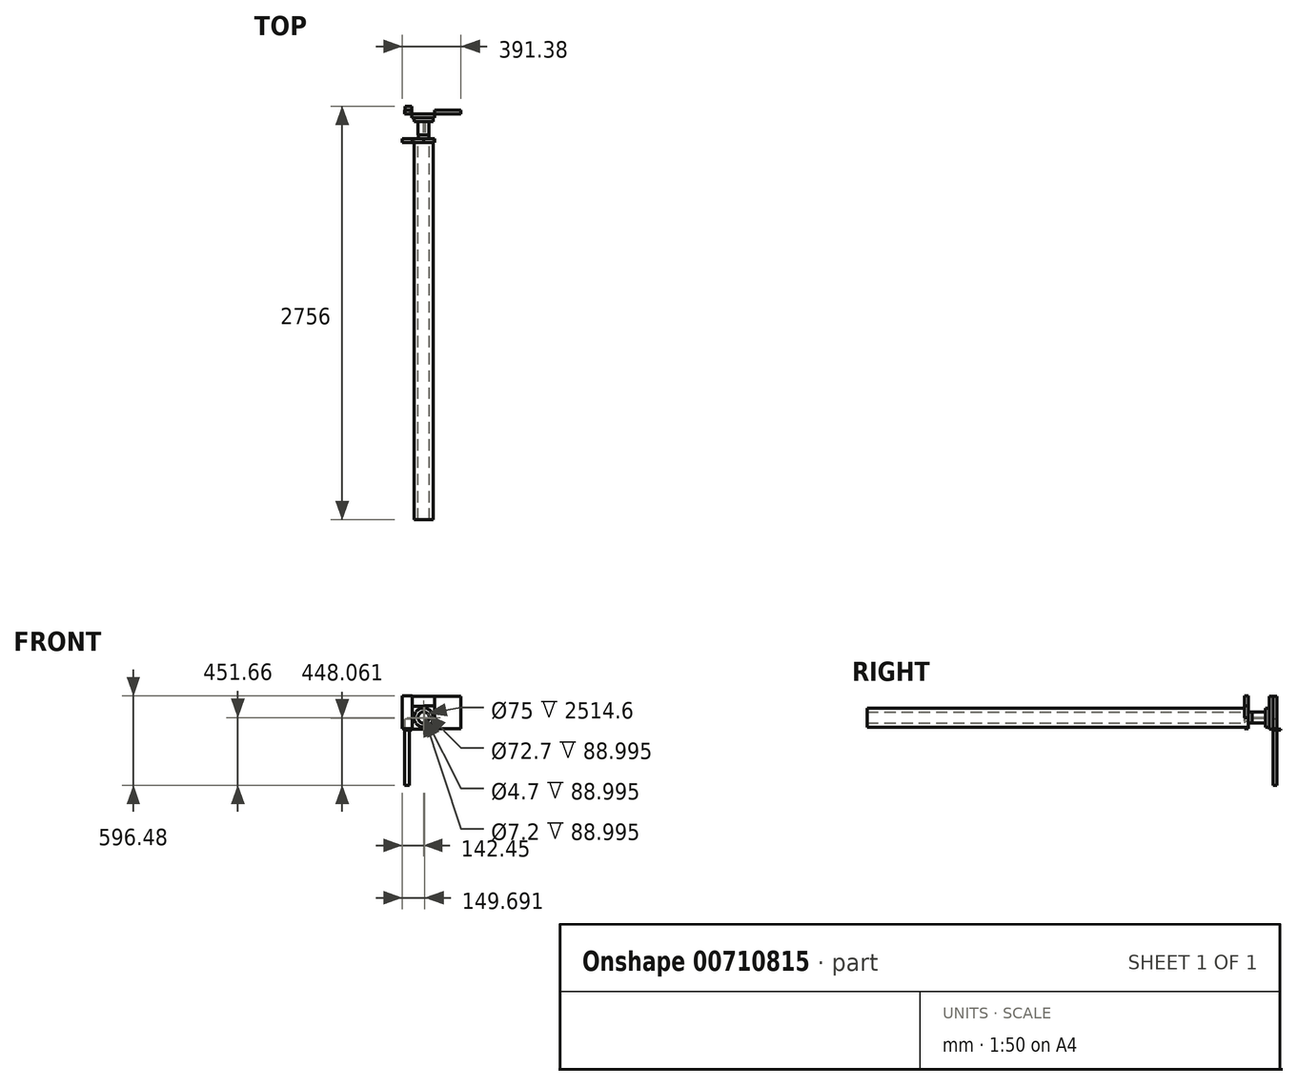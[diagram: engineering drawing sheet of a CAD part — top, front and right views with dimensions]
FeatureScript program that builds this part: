
annotation { "Feature Type Name" : "Feature", "Feature Type Description" : "" }
export const myFeature = defineFeature(function(context is Context, id is Id, definition is map)
    precondition{}
    {
        {
            var Q0;
            Q0=qCreatedBy(makeId("Front.planeOp"),FACE);
            var sketch = newSketch(context, id + "F0", { "sketchPlane" : qUnion([Q0])});
            skCircle(sketch, "E0", {"center": v(0, 0) * mm, "radius": 63.5 * mm});
            skSolve(sketch);
        }
        {
            var Q0;
            Q0 = qSketchRegion(id + "F0", true);
            extrude(context, id + "F1", {"entities" : qUnion([Q0]), "depth" : 2540 * mm, "offsetDistance" : 25.4 * mm});
        }
        {
            var Q0;
            Q0=makeQuery(id+"F1.opExtrude","CAP_FACE",FACE,{"disambiguationData":[OSD([sQuery(id+"F0.wireOp",EDGE,"E0")])],"isStart":true});
            var sketch = newSketch(context, id + "F2", { "sketchPlane" : qUnion([Q0])});
            skCircle(sketch, "E1", {"center": v(0, 0) * mm, "radius": 37.5 * mm});
            skSolve(sketch);
        }
        {
            var Q0;
            Q0=makeQuery(id+"F2.imprint","IMPRINT",FACE,{"disambiguationData":[TD([[makeQuery(id+"F2.imprint","IMPRINT",EDGE,{"derivedFrom":sQuery(id+"F2.wireOp",EDGE,"E1")}),1.0]])]});
            extrude(context, id + "F3", {"entities" : qUnion([Q0]), "operationType" : NewBodyOperationType.REMOVE, "endBound" : BoundingType.THROUGH_ALL, "oppositeDirection" : true, "depth" : 25.4 * mm, "offsetDistance" : 25.4 * mm});
        }
        {
            var Q0;
            Q0=makeQuery(id+"F1.opExtrude","CAP_FACE",FACE,{"disambiguationData":[OSD([sQuery(id+"F0.wireOp",EDGE,"E0")])],"isStart":true});
            var sketch = newSketch(context, id + "F4", { "sketchPlane" : qUnion([Q0])});
            skCircle(sketch, "E2.0", {"center": v(0, 0) * mm, "radius": 37.5 * mm});
            skSolve(sketch);
        }
        {
            var Q0;
            Q0 = qSketchRegion(id + "F4", true);
            extrude(context, id + "F5", {"entities" : qUnion([Q0]), "operationType" : NewBodyOperationType.ADD, "oppositeDirection" : true, "depth" : 25.4 * mm, "offsetDistance" : 25.4 * mm});
        }
        {
            var Q0;
            Q0=makeQuery(id+"F5.boolean.opBoolean","MERGE",FACE,{"derivedFrom":[makeQuery(id+"F1.opExtrude","CAP_FACE",FACE,{"disambiguationData":[OSD([sQuery(id+"F0.wireOp",EDGE,"E0")])],"isStart":true}),makeQuery(id+"F5.opExtrude","CAP_FACE",FACE,{"disambiguationData":[OSD([sQuery(id+"F4.wireOp",EDGE,"E2.0")])],"isStart":true})]});
            var sketch = newSketch(context, id + "F6", { "sketchPlane" : qUnion([Q0])});
            skCircle(sketch, "E3", {"center": v(0, 0) * mm, "radius": 35.8 * mm});
            skSolve(sketch);
        }
        {
            var Q0;
            Q0 = qSketchRegion(id + "F6", true);
            extrude(context, id + "F7", {"entities" : qUnion([Q0]), "operationType" : NewBodyOperationType.ADD, "depth" : 25.4 * mm, "offsetDistance" : 25.4 * mm});
        }
        {
            var Q0;
            Q0=makeQuery(id+"F7.opExtrude","CAP_FACE",FACE,{"disambiguationData":[OSD([sQuery(id+"F6.wireOp",EDGE,"E3")])],"isStart":false});
            var sketch = newSketch(context, id + "F8", { "sketchPlane" : qUnion([Q0])});
            skCircle(sketch, "E4", {"center": v(0, 0) * mm, "radius": 35.83 * mm});
            skCircle(sketch, "E5", {"center": v(0, 0) * mm, "radius": 36.12 * mm});
            skCircle(sketch, "E6", {"center": v(0, -3.6) * mm, "radius": 3.6 * mm});
            skCircle(sketch, "E7", {"center": v(0, 0) * mm, "radius": 36.35 * mm});
            skCircle(sketch, "E8", {"center": v(0, 0) * mm, "radius": 36.4 * mm});
            skCircle(sketch, "E9", {"center": v(-7.24, -3.6) * mm, "radius": 2.35 * mm});
            skSolve(sketch);
        }
        {
            var Q0;
            Q0=makeQuery(id+"F8.imprint","IMPRINT",FACE,{"disambiguationData":[TD([[makeQuery(id+"F8.imprint","IMPRINT",EDGE,{"derivedFrom":sQuery(id+"F8.wireOp",EDGE,"E7")}),-1.0]])]});
            var Q1;
            Q1=makeQuery(id+"F8.imprint","IMPRINT",FACE,{"disambiguationData":[TD([[makeQuery(id+"F8.imprint","IMPRINT",EDGE,{"derivedFrom":sQuery(id+"F8.wireOp",EDGE,"E6")}),-1.0]])]});
            extrude(context, id + "F9", {"entities" : qUnion([Q0, Q1]), "operationType" : NewBodyOperationType.ADD, "depth" : 89 * mm, "offsetDistance" : 25.4 * mm});
        }
        {
            var Q0;
            Q0=makeQuery(id+"F9.opExtrude","CAP_FACE",FACE,{"disambiguationData":[OSD([sQuery(id+"F6.wireOp",EDGE,"E3"),sQuery(id+"F8.wireOp",EDGE,"E6"),sQuery(id+"F8.wireOp",EDGE,"E9")])],"isStart":false});
            var sketch = newSketch(context, id + "F10", { "sketchPlane" : qUnion([Q0])});
            skCircle(sketch, "E10.0.0", {"center": v(0, 0) * mm, "radius": 63.5 * mm});
            skSolve(sketch);
        }
        {
            var Q0;
            Q0 = qSketchRegion(id + "F10", true);
            extrude(context, id + "F11", {"entities" : qUnion([Q0]), "operationType" : NewBodyOperationType.ADD, "depth" : 25.4 * mm, "offsetDistance" : 25.4 * mm});
        }
        {
            var Q0;
            Q0=makeQuery(id+"F11.opExtrude","CAP_FACE",FACE,{"disambiguationData":[OSD([sQuery(id+"F10.wireOp",EDGE,"E10.0.0")])],"isStart":false});
            var sketch = newSketch(context, id + "F12", { "sketchPlane" : qUnion([Q0])});
            skCircle(sketch, "E11", {"center": v(0, 0) * mm, "radius": 63.43 * mm});
            skSolve(sketch);
        }
        {
            var Q0;
            Q0=qCreatedBy(makeId("Front.planeOp"),FACE);
            var sketch = newSketch(context, id + "F13", { "sketchPlane" : qUnion([Q0])});
            skLineSegment(sketch, "E12.bottom", {"start": v(0, -29.35) * mm, "end": v(-76.58, -29.35) * mm});
            skLineSegment(sketch, "E12.top", {"start": v(0, 73.7) * mm, "end": v(-76.58, 73.7) * mm});
            skLineSegment(sketch, "E12.left", {"start": v(0, -29.35) * mm, "end": v(0, 73.7) * mm});
            skLineSegment(sketch, "E12.right", {"start": v(-76.58, -29.35) * mm, "end": v(-76.58, 73.7) * mm});
            skSolve(sketch);
        }
        {
            var Q0;
            Q0=makeQuery(id+"F13.imprint","IMPRINT",FACE,{"disambiguationData":[TD([[makeQuery(id+"F13.imprint","IMPRINT",EDGE,{"derivedFrom":sQuery(id+"F13.wireOp",EDGE,"E12.bottom")}),-1.0]])]});
            var sketch = newSketch(context, id + "F14", { "sketchPlane" : qUnion([Q0])});
            skLineSegment(sketch, "E13.bottom", {"start": v(0, -28.92) * mm, "end": v(75.18, -28.92) * mm});
            skLineSegment(sketch, "E13.top", {"start": v(0, 76.32) * mm, "end": v(75.18, 76.32) * mm});
            skLineSegment(sketch, "E13.left", {"start": v(0, -28.92) * mm, "end": v(0, 76.32) * mm});
            skLineSegment(sketch, "E13.right", {"start": v(75.18, -28.92) * mm, "end": v(75.18, 76.32) * mm});
            skSolve(sketch);
        }
        {
            var Q0;
            {var subQ3=sQuery(id+"F14.wireOp",EDGE,"E13.bottom");Q0=makeQuery(id+"F14.imprint","IMPRINT",FACE,{"disambiguationData":[TD([[makeQuery(id+"F14.imprint","IMPRINT",EDGE,{"derivedFrom":subQ3}),1.0]])]});}
            var sketch = newSketch(context, id + "F15", { "sketchPlane" : qUnion([Q0])});
            skLineSegment(sketch, "E14.bottom", {"start": v(0, -22.3) * mm, "end": v(-75.63, -22.3) * mm});
            skLineSegment(sketch, "E14.top", {"start": v(0, 74.56) * mm, "end": v(-75.63, 74.56) * mm});
            skLineSegment(sketch, "E14.left", {"start": v(0, -22.3) * mm, "end": v(0, 74.56) * mm});
            skLineSegment(sketch, "E14.right", {"start": v(-75.63, -22.3) * mm, "end": v(-75.63, 74.56) * mm});
            skSolve(sketch);
        }
        {
            var Q0;
            Q0 = qSketchRegion(id + "F15", true);
            extrude(context, id + "F16", {"entities" : qUnion([Q0]), "operationType" : NewBodyOperationType.ADD, "depth" : 25.4 * mm, "offsetDistance" : 25.4 * mm});
        }
        {
            var Q0;
            {var subQ3=sQuery(id+"F14.wireOp",EDGE,"E13.bottom");Q0=makeQuery(id+"F14.imprint","IMPRINT",FACE,{"disambiguationData":[TD([[makeQuery(id+"F14.imprint","IMPRINT",EDGE,{"derivedFrom":subQ3}),1.0]])]});}
            var sketch = newSketch(context, id + "F17", { "sketchPlane" : qUnion([Q0])});
            skLineSegment(sketch, "E15.bottom", {"start": v(0, 0) * mm, "end": v(71.74, 0) * mm});
            skLineSegment(sketch, "E15.top", {"start": v(0, 76.94) * mm, "end": v(71.74, 76.94) * mm});
            skLineSegment(sketch, "E15.left", {"start": v(0, 0) * mm, "end": v(0, 76.94) * mm});
            skLineSegment(sketch, "E15.right", {"start": v(71.74, 0) * mm, "end": v(71.74, 76.94) * mm});
            skSolve(sketch);
        }
        {
            var Q0;
            Q0 = qSketchRegion(id + "F17", true);
            extrude(context, id + "F18", {"entities" : qUnion([Q0]), "operationType" : NewBodyOperationType.ADD, "depth" : 25.4 * mm, "offsetDistance" : 25.4 * mm});
        }
        {
            var Q0;
            Q0=qCreatedBy(makeId("Front.planeOp"),FACE);
            var sketch = newSketch(context, id + "F19", { "sketchPlane" : qUnion([Q0])});
            skLineSegment(sketch, "E16.bottom", {"start": v(-75.77, -75.26) * mm, "end": v(-142.45, -75.26) * mm});
            skLineSegment(sketch, "E16.top", {"start": v(-75.77, 144.82) * mm, "end": v(-142.45, 144.82) * mm});
            skLineSegment(sketch, "E16.left", {"start": v(-75.77, -75.26) * mm, "end": v(-75.77, 144.82) * mm});
            skLineSegment(sketch, "E16.right", {"start": v(-142.45, -75.26) * mm, "end": v(-142.45, 144.82) * mm});
            skSolve(sketch);
        }
        {
            var Q0;
            Q0 = qSketchRegion(id + "F19", true);
            extrude(context, id + "F20", {"entities" : qUnion([Q0]), "depth" : 25.4 * mm, "offsetDistance" : 25.4 * mm});
        }
        {
            var Q0;
            Q0=makeQuery(id+"F12.imprint","IMPRINT",FACE,{"disambiguationData":[TD([[makeQuery(id+"F12.imprint","IMPRINT",EDGE,{"derivedFrom":sQuery(id+"F12.wireOp",EDGE,"E11")}),1.0]])]});
            var sketch = newSketch(context, id + "F21", { "sketchPlane" : qUnion([Q0])});
            skLineSegment(sketch, "E17.bottom", {"start": v(78.01, 142.55) * mm, "end": v(-73.8, 142.55) * mm});
            skLineSegment(sketch, "E17.top", {"start": v(78.01, -76.44) * mm, "end": v(-73.8, -76.44) * mm});
            skLineSegment(sketch, "E17.left", {"start": v(78.01, 142.55) * mm, "end": v(78.01, -76.44) * mm});
            skLineSegment(sketch, "E17.right", {"start": v(-73.8, 142.55) * mm, "end": v(-73.8, -76.44) * mm});
            skSolve(sketch);
        }
        {
            var Q0;
            Q0 = qSketchRegion(id + "F21", true);
            extrude(context, id + "F22", {"entities" : qUnion([Q0]), "operationType" : NewBodyOperationType.ADD, "depth" : 25.4 * mm, "offsetDistance" : 25.4 * mm});
        }
        {
            var Q0;
            Q0=makeQuery(id+"F22.opExtrude","CAP_FACE",FACE,{"disambiguationData":[OSD([sQuery(id+"F21.wireOp",EDGE,"E17.bottom"),sQuery(id+"F21.wireOp",EDGE,"E17.top"),sQuery(id+"F21.wireOp",EDGE,"E17.left"),sQuery(id+"F21.wireOp",EDGE,"E17.right")])],"isStart":false});
            var sketch = newSketch(context, id + "F23", { "sketchPlane" : qUnion([Q0])});
            skLineSegment(sketch, "E18.bottom", {"start": v(-73.8, 142.55) * mm, "end": v(-248.93, 142.55) * mm});
            skLineSegment(sketch, "E18.top", {"start": v(-73.8, -74.3) * mm, "end": v(-248.93, -74.3) * mm});
            skLineSegment(sketch, "E18.left", {"start": v(-73.8, 142.55) * mm, "end": v(-73.8, -74.3) * mm});
            skLineSegment(sketch, "E18.right", {"start": v(-248.93, 142.55) * mm, "end": v(-248.93, -74.3) * mm});
            skSolve(sketch);
        }
        {
            var Q0;
            Q0 = qSketchRegion(id + "F23", true);
            extrude(context, id + "F24", {"entities" : qUnion([Q0]), "depth" : 25.4 * mm, "offsetDistance" : 25.4 * mm});
        }
        {
            var Q0;
            Q0=makeQuery(id+"F22.opExtrude","CAP_FACE",FACE,{"disambiguationData":[OSD([sQuery(id+"F21.wireOp",EDGE,"E17.bottom"),sQuery(id+"F21.wireOp",EDGE,"E17.top"),sQuery(id+"F21.wireOp",EDGE,"E17.left"),sQuery(id+"F21.wireOp",EDGE,"E17.right")])],"isStart":false});
            var sketch = newSketch(context, id + "F25", { "sketchPlane" : qUnion([Q0])});
            skLineSegment(sketch, "E19.bottom", {"start": v(126.2, -83.37) * mm, "end": v(93.65, -83.37) * mm});
            skLineSegment(sketch, "E19.top", {"start": v(126.2, -451.66) * mm, "end": v(93.65, -451.66) * mm});
            skLineSegment(sketch, "E19.left", {"start": v(126.2, -83.37) * mm, "end": v(126.2, -451.66) * mm});
            skLineSegment(sketch, "E19.right", {"start": v(93.65, -83.37) * mm, "end": v(93.65, -451.66) * mm});
            skSolve(sketch);
        }
        {
            var Q0;
            Q0 = qSketchRegion(id + "F25", true);
            extrude(context, id + "F26", {"entities" : qUnion([Q0]), "depth" : 25.4 * mm, "offsetDistance" : 25.4 * mm});
        }
        {
            var Q0;
            Q0=makeQuery(id+"F22.opExtrude","CAP_FACE",FACE,{"disambiguationData":[OSD([sQuery(id+"F21.wireOp",EDGE,"E17.bottom"),sQuery(id+"F21.wireOp",EDGE,"E17.top"),sQuery(id+"F21.wireOp",EDGE,"E17.left"),sQuery(id+"F21.wireOp",EDGE,"E17.right")])],"isStart":false});
            var sketch = newSketch(context, id + "F27", { "sketchPlane" : qUnion([Q0])});
            skLineSegment(sketch, "E20.bottom", {"start": v(78.01, -76.44) * mm, "end": v(124.52, -76.44) * mm});
            skLineSegment(sketch, "E20.top", {"start": v(78.01, -10.69) * mm, "end": v(124.52, -10.69) * mm});
            skLineSegment(sketch, "E20.left", {"start": v(78.01, -76.44) * mm, "end": v(78.01, -10.69) * mm});
            skLineSegment(sketch, "E20.right", {"start": v(124.52, -76.44) * mm, "end": v(124.52, -10.69) * mm});
            skSolve(sketch);
        }
        {
            var Q0;
            Q0 = qSketchRegion(id + "F27", true);
            extrude(context, id + "F28", {"entities" : qUnion([Q0]), "depth" : 25.4 * mm, "offsetDistance" : 25.4 * mm});
        }
        {
            var Q0;
            Q0=makeQuery(id+"F28.opExtrude","CAP_FACE",FACE,{"disambiguationData":[OSD([sQuery(id+"F27.wireOp",EDGE,"E20.bottom"),sQuery(id+"F27.wireOp",EDGE,"E20.top"),sQuery(id+"F27.wireOp",EDGE,"E20.left"),sQuery(id+"F27.wireOp",EDGE,"E20.right")])],"isStart":false});
            var sketch = newSketch(context, id + "F29", { "sketchPlane" : qUnion([Q0])});
            skLineSegment(sketch, "E21.bottom", {"start": v(78.01, -76.44) * mm, "end": v(124.52, -76.44) * mm});
            skLineSegment(sketch, "E21.top", {"start": v(78.01, -84.55) * mm, "end": v(124.52, -84.55) * mm});
            skLineSegment(sketch, "E21.left", {"start": v(78.01, -76.44) * mm, "end": v(78.01, -84.55) * mm});
            skLineSegment(sketch, "E21.right", {"start": v(124.52, -76.44) * mm, "end": v(124.52, -84.55) * mm});
            skSolve(sketch);
        }
        {
            var Q0;
            Q0 = qSketchRegion(id + "F29", true);
            extrude(context, id + "F30", {"entities" : qUnion([Q0]), "operationType" : NewBodyOperationType.ADD, "depth" : 25.4 * mm, "offsetDistance" : 25.4 * mm});
        }
    });
